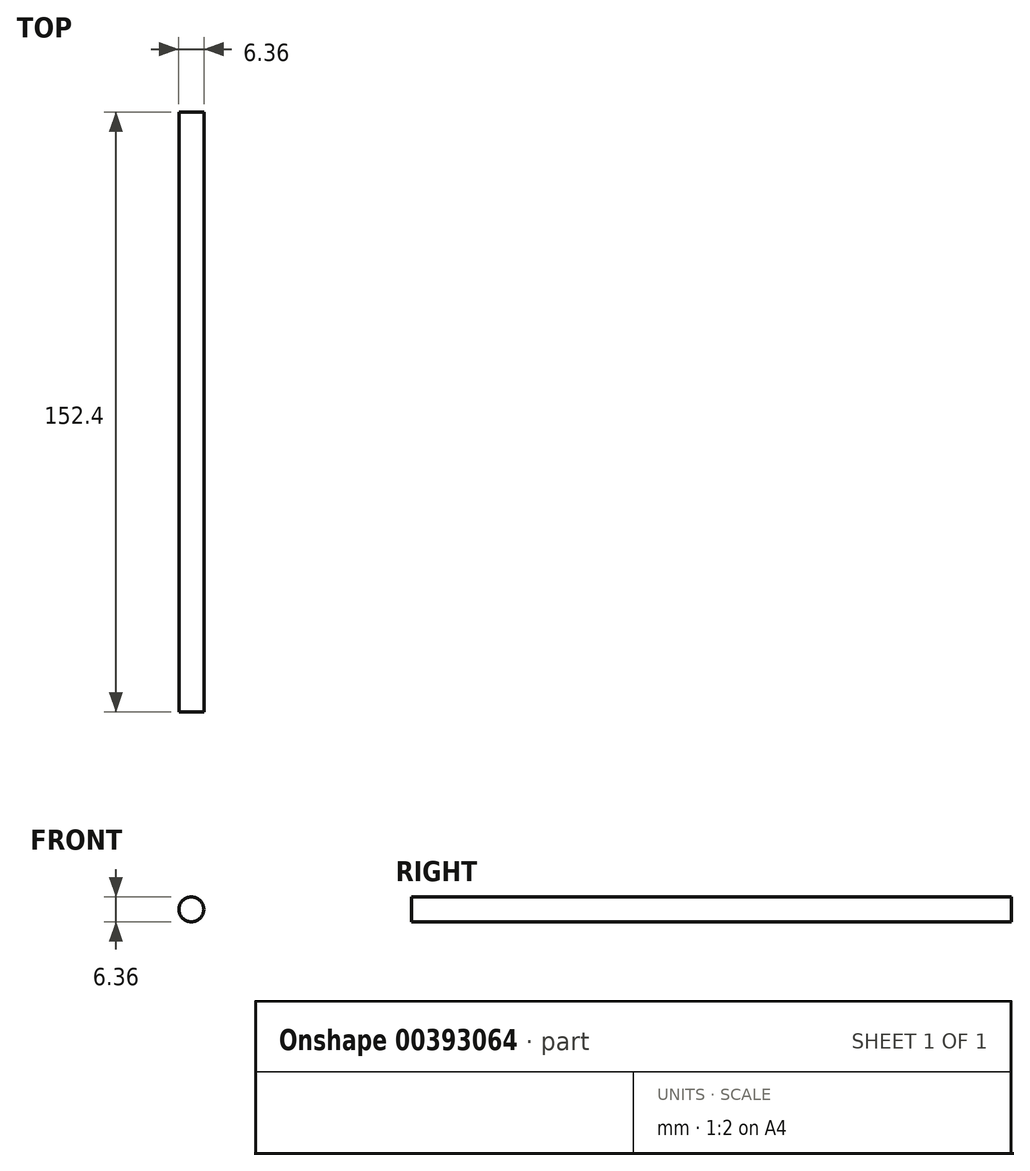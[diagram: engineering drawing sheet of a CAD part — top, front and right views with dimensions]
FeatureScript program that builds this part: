
annotation { "Feature Type Name" : "Feature", "Feature Type Description" : "" }
export const myFeature = defineFeature(function(context is Context, id is Id, definition is map)
    precondition{}
    {
        {
            var Q0;
            Q0=qCreatedBy(makeId("Front.planeOp"),FACE);
            var sketch = newSketch(context, id + "F0", { "sketchPlane" : qUnion([Q0])});
            skCircle(sketch, "E0", {"center": v(0, 0) * mm, "radius": 3.18 * mm});
            skSolve(sketch);
        }
        {
            var Q0;
            Q0=makeQuery(id+"F0.imprint","IMPRINT",FACE,{"disambiguationData":[TD([[makeQuery(id+"F0.imprint","IMPRINT",EDGE,{"derivedFrom":sQuery(id+"F0.wireOp",EDGE,"E0")}),1.0]])]});
            extrude(context, id + "F1", {"entities" : qUnion([Q0]), "depth" : 152.4 * mm});
        }
    });
